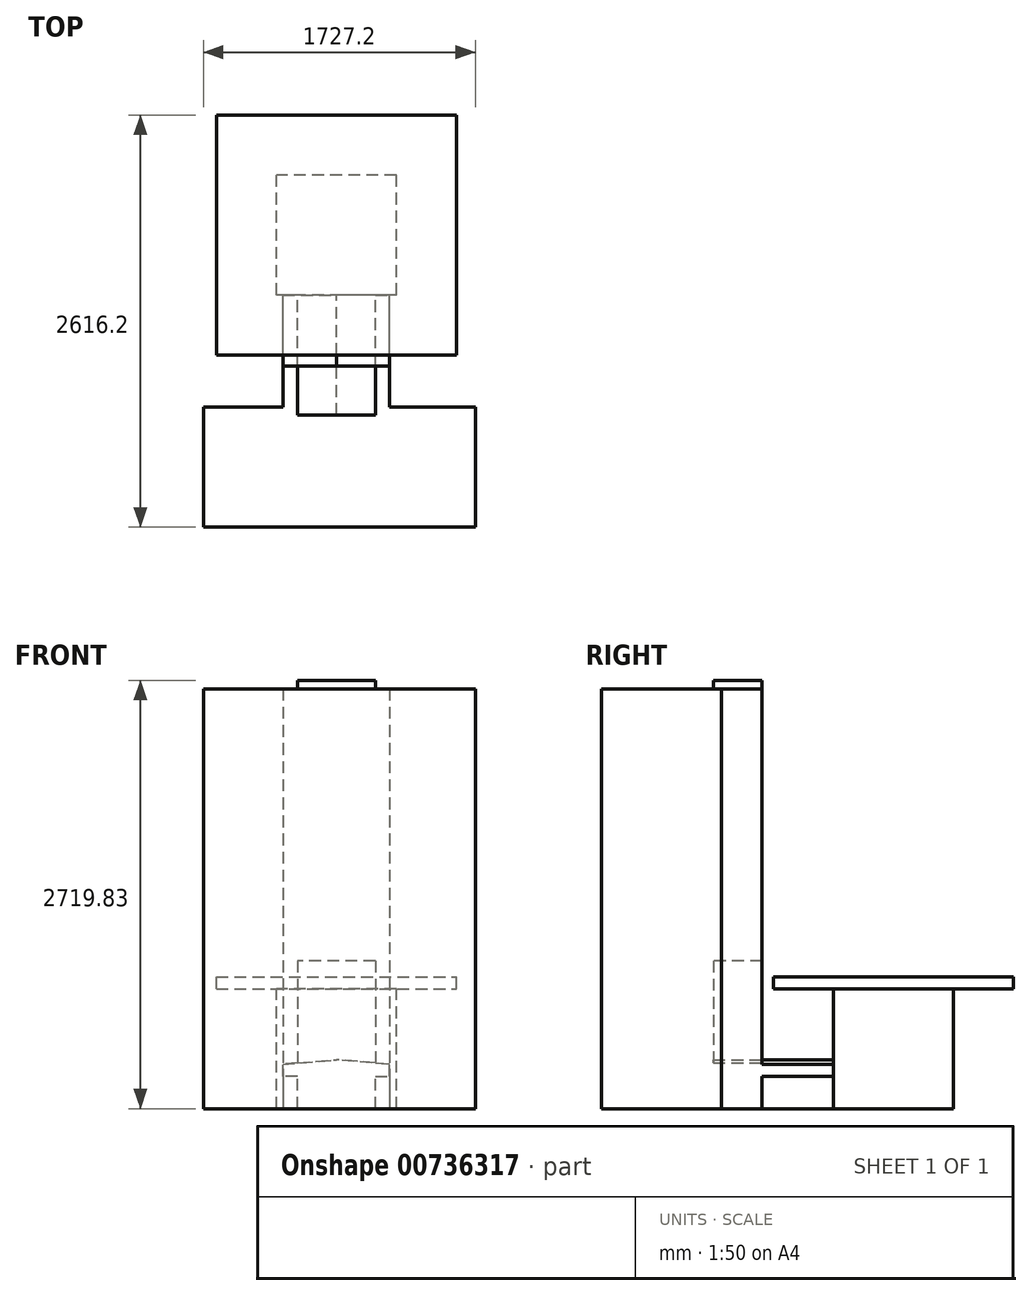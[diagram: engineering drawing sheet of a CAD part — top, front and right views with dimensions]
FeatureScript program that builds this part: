
annotation { "Feature Type Name" : "Feature", "Feature Type Description" : "" }
export const myFeature = defineFeature(function(context is Context, id is Id, definition is map)
    precondition{}
    {
        {
            var Q0;
            Q0=qCreatedBy(makeId("Top.planeOp"),FACE);
            var sketch = newSketch(context, id + "F0", { "sketchPlane" : qUnion([Q0])});
            skLineSegment(sketch, "E0.bottom", {"start": v(-762, -762) * mm, "end": v(762, -762) * mm});
            skLineSegment(sketch, "E0.top", {"start": v(-762, 762) * mm, "end": v(762, 762) * mm});
            skLineSegment(sketch, "E0.left", {"start": v(-762, -762) * mm, "end": v(-762, 762) * mm});
            skLineSegment(sketch, "E0.right", {"start": v(762, -762) * mm, "end": v(762, 762) * mm});
            skSolve(sketch);
        }
        {
            var Q0;
            Q0=makeQuery(id+"F0.imprint","IMPRINT",FACE,{"disambiguationData":[TD([[makeQuery(id+"F0.imprint","IMPRINT",EDGE,{"derivedFrom":sQuery(id+"F0.wireOp",EDGE,"E0.bottom")}),1.0]])]});
            extrude(context, id + "F1", {"entities" : qUnion([Q0]), "oppositeDirection" : true, "depth" : 76.2 * mm, "offsetDistance" : 25.4 * mm});
        }
        {
            var Q0;
            Q0=makeQuery(id+"F1.opExtrude","CAP_FACE",FACE,{"disambiguationData":[OSD([sQuery(id+"F0.wireOp",EDGE,"E0.bottom"),sQuery(id+"F0.wireOp",EDGE,"E0.top"),sQuery(id+"F0.wireOp",EDGE,"E0.left"),sQuery(id+"F0.wireOp",EDGE,"E0.right")])],"isStart":false});
            var sketch = newSketch(context, id + "F2", { "sketchPlane" : qUnion([Q0])});
            skLineSegment(sketch, "E1.bottom", {"start": v(381, 381) * mm, "end": v(-381, 381) * mm});
            skLineSegment(sketch, "E1.top", {"start": v(381, -381) * mm, "end": v(-381, -381) * mm});
            skLineSegment(sketch, "E1.left", {"start": v(381, 381) * mm, "end": v(381, -381) * mm});
            skLineSegment(sketch, "E1.right", {"start": v(-381, 381) * mm, "end": v(-381, -381) * mm});
            skSolve(sketch);
        }
        {
            var Q0;
            Q0 = qSketchRegion(id + "F2", true);
            extrude(context, id + "F3", {"entities" : qUnion([Q0]), "operationType" : NewBodyOperationType.ADD, "depth" : 762 * mm, "offsetDistance" : 25.4 * mm});
        }
        {
            var Q0;
            Q0=makeQuery(id+"F3.opExtrude","SWEPT_FACE",FACE,{"disambiguationData":[OSD([sQuery(id+"F2.wireOp",EDGE,"E1.bottom")])]});
            var sketch = newSketch(context, id + "F4", { "sketchPlane" : qUnion([Q0])});
            skLineSegment(sketch, "E2", {"start": v(-247.9, -838.2) * mm, "end": v(-247.9, -633.96) * mm});
            skLineSegment(sketch, "E3", {"start": v(-247.9, -633.96) * mm, "end": v(-339.19, -633.96) * mm});
            skLineSegment(sketch, "E4", {"start": v(-339.19, -633.96) * mm, "end": v(-339.19, -555.35) * mm});
            skLineSegment(sketch, "E5", {"start": v(-339.19, -555.35) * mm, "end": v(0, -527.45) * mm});
            skLineSegment(sketch, "E6", {"start": v(0, 0) * mm, "end": v(0, -838.2) * mm, "construction": true});
            skLineSegment(sketch, "E7.MirrorCS", {"start": v(247.9, -838.2) * mm, "end": v(247.9, -633.96) * mm});
            skLineSegment(sketch, "E8.MirrorCS", {"start": v(247.9, -633.96) * mm, "end": v(339.19, -633.96) * mm});
            skLineSegment(sketch, "E9.MirrorCS", {"start": v(339.19, -555.35) * mm, "end": v(0, -527.45) * mm});
            skLineSegment(sketch, "E10.MirrorCS", {"start": v(339.19, -633.96) * mm, "end": v(339.19, -555.35) * mm});
            skLineSegment(sketch, "E11", {"start": v(-247.9, -838.2) * mm, "end": v(247.9, -838.2) * mm});
            skSolve(sketch);
        }
        {
            var Q0;
            Q0 = qSketchRegion(id + "F4", true);
            extrude(context, id + "F5", {"entities" : qUnion([Q0]), "operationType" : NewBodyOperationType.ADD, "depth" : 762 * mm, "offsetDistance" : 25.4 * mm});
        }
        {
            var Q0;
            Q0=makeQuery(id+"F5.boolean.opBoolean","MERGE",FACE,{"derivedFrom":[makeQuery(id+"F3.opExtrude","CAP_FACE",FACE,{"disambiguationData":[OSD([sQuery(id+"F2.wireOp",EDGE,"E1.bottom"),sQuery(id+"F2.wireOp",EDGE,"E1.top"),sQuery(id+"F2.wireOp",EDGE,"E1.left"),sQuery(id+"F2.wireOp",EDGE,"E1.right")])],"isStart":false}),makeQuery(id+"F5.opExtrude","SWEPT_FACE",FACE,{"disambiguationData":[OSD([sQuery(id+"F4.wireOp",EDGE,"E11")])]})]});
            var sketch = newSketch(context, id + "F6", { "sketchPlane" : qUnion([Q0])});
            skLineSegment(sketch, "E12.bottom", {"start": v(882.9, 1854.2) * mm, "end": v(-844.3, 1854.2) * mm});
            skLineSegment(sketch, "E12.top", {"start": v(882.9, 1092.2) * mm, "end": v(339.19, 1092.2) * mm});
            skLineSegment(sketch, "E12.left", {"start": v(882.9, 1854.2) * mm, "end": v(882.9, 1092.2) * mm});
            skLineSegment(sketch, "E12.right", {"start": v(-844.3, 1854.2) * mm, "end": v(-844.3, 1092.2) * mm});
            skLineSegment(sketch, "E13", {"start": v(-339.19, 1092.2) * mm, "end": v(-339.19, 833.12) * mm});
            skLineSegment(sketch, "E14", {"start": v(-339.19, 833.12) * mm, "end": v(339.19, 833.12) * mm});
            skLineSegment(sketch, "E15", {"start": v(339.19, 833.12) * mm, "end": v(339.19, 1092.2) * mm});
            skLineSegment(sketch, "E16.trimOffspring", {"start": v(-339.19, 1092.2) * mm, "end": v(-844.3, 1092.2) * mm});
            skSolve(sketch);
        }
        {
            var Q0;
            Q0=makeQuery(id+"F6.imprint","IMPRINT",FACE,{"disambiguationData":[TD([[makeQuery(id+"F6.imprint","IMPRINT",EDGE,{"derivedFrom":sQuery(id+"F6.wireOp",EDGE,"E12.bottom")}),1.0]])]});
            extrude(context, id + "F7", {"entities" : qUnion([Q0]), "operationType" : NewBodyOperationType.ADD, "oppositeDirection" : true, "depth" : 2667 * mm, "offsetDistance" : 25.4 * mm});
        }
        {
            var Q0;
            Q0=makeQuery(id+"F7.opExtrude","SWEPT_FACE",FACE,{"disambiguationData":[OSD([sQuery(id+"F4.wireOp",EDGE,"E11")])]});
            var sketch = newSketch(context, id + "F8", { "sketchPlane" : qUnion([Q0])});
            skLineSegment(sketch, "E17.bottom", {"start": v(-247.9, 1881.63) * mm, "end": v(247.9, 1881.63) * mm});
            skLineSegment(sketch, "E17.top", {"start": v(-247.9, 101.6) * mm, "end": v(247.9, 101.6) * mm});
            skLineSegment(sketch, "E17.left", {"start": v(-247.9, 1881.63) * mm, "end": v(-247.9, 101.6) * mm});
            skLineSegment(sketch, "E17.right", {"start": v(247.9, 1881.63) * mm, "end": v(247.9, 101.6) * mm});
            skSolve(sketch);
        }
        {
            var Q0;
            Q0 = qSketchRegion(id + "F8", true);
            var Q1;
            {var subQ0=sQuery(id+"F6.wireOp",EDGE,"E14");var subQ1=sQuery(id+"F6.wireOp",EDGE,"E13");Q1=makeQuery(id+"F7.boolean.opBoolean","SPLIT",FACE,{"disambiguationData":[TD([makeQuery(id+"F5.opExtrude","SWEPT_FACE",FACE,{"disambiguationData":[OSD([sQuery(id+"F4.wireOp",EDGE,"E5")])]})])],"derivedFrom":makeQuery(id+"F7.opExtrude","SWEPT_FACE",FACE,{"disambiguationData":[OSD([subQ0]),TDD([makeQuery(id+"F6.imprint","IMPRINT",EDGE,{"disambiguationData":[TD([[makeQuery(id+"F6.imprint","INTERSECT",VERTEX,{"derivedFrom":[subQ1,subQ0]}),-1.0]])],"derivedFrom":subQ0})])]})});}
            extrude(context, id + "F9", {"entities" : qUnion([Q0]), "operationType" : NewBodyOperationType.ADD, "endBound" : BoundingType.UP_TO_SURFACE, "depth" : 25.4 * mm, "endBoundEntityFace" : qUnion([Q1]), "offsetDistance" : 25.4 * mm});
        }
    });
